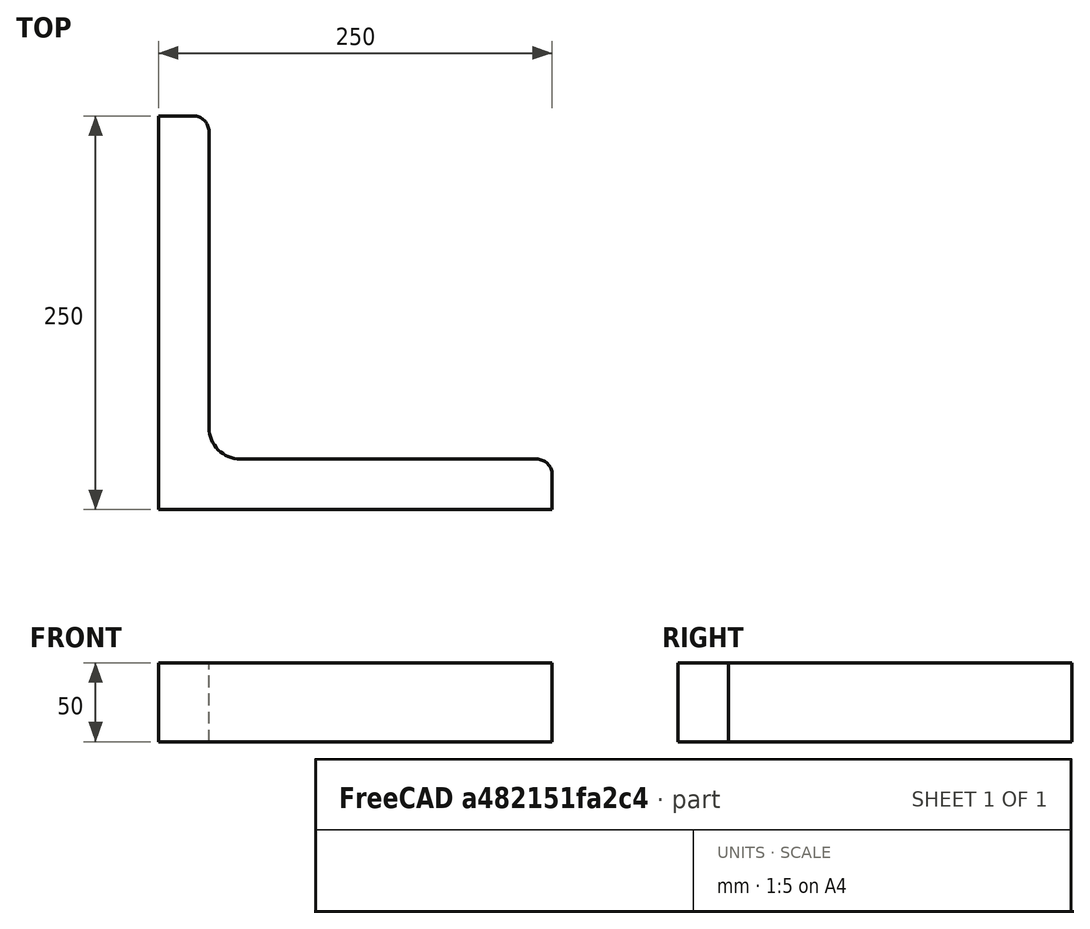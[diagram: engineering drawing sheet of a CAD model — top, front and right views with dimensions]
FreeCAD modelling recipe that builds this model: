
FCSTD DOCUMENT  (FreeCAD 0.15R4671 (Git))
Label: Angle Bar L250x250x32 EN10056 S235JR
License: All rights reserved
LicenseURL: http://en.wikipedia.org/wiki/All_rights_reserved
objects: Sketcher::SketchObject×1, Part::Extrusion×1
note: 2 computed .brp shape members not serialized (recipe doc carries the construction recipe); baked Part::Feature solids carry a one-line shape summary decoded from their .brp

FEATURE [Sketcher::SketchObject] Sketch
  sketch-geometry (9):
    g0: LineSegment StartX=0 StartY=0 StartZ=0 EndX=250 EndY=0 EndZ=0
    g1: LineSegment StartX=250 StartY=0 StartZ=0 EndX=250 EndY=22 EndZ=0
    g2: LineSegment StartX=240 StartY=32 StartZ=0 EndX=52 EndY=32 EndZ=0
    g3: LineSegment StartX=0 StartY=0 StartZ=0 EndX=0 EndY=250 EndZ=0
    g4: LineSegment StartX=0 StartY=250 StartZ=0 EndX=22 EndY=250 EndZ=0
    g5: LineSegment StartX=32 StartY=240 StartZ=0 EndX=32 EndY=52 EndZ=0
    g6: ArcOfCircle CenterX=52 CenterY=52 CenterZ=0 NormalX=0 NormalY=0 NormalZ=1 Radius=20 StartAngle=3.14159 EndAngle=4.71239
    g7: ArcOfCircle CenterX=22 CenterY=240 CenterZ=0 NormalX=0 NormalY=0 NormalZ=1 Radius=10 StartAngle=0 EndAngle=1.5708
    g8: ArcOfCircle CenterX=240 CenterY=22 CenterZ=0 NormalX=0 NormalY=0 NormalZ=1 Radius=10 StartAngle=0 EndAngle=1.5708
  constraints (23):
    c: Coincident(g0,g-1)
    c: Horizontal(g0)
    c: Coincident(g1,g0)
    c: Vertical(g1)
    c: Horizontal(g2)
    c: Coincident(g3,g-1)
    c: Vertical(g3)
    c: Coincident(g4,g3)
    c: Horizontal(g4)
    c: Vertical(g5)
    c: Tangent(g5,g6) = -1.5708
    c: Tangent(g2,g6) = 1.5708
    c: Tangent(g4,g7) = 1.5708
    c: Tangent(g5,g7) = 1.5708
    c: Tangent(g2,g8) = -1.5708
    c: Tangent(g1,g8) = -1.5708
    c: DistanceX(g0) = 250
    c: DistanceY(g3) = 250
    c: DistanceY(g0,g2) = 32
    c: DistanceX(g3,g5) = 32
    c: Radius(g6) = 20
    c: Radius(g8) = 10
    c: Radius(g7) = 10
FEATURE [Part::Extrusion] Extrude  label="Angle Bar L250x250x32 EN10056 S235JR"
  Base = -> Sketch
  Dir = (0,0,50)
  Solid = true
